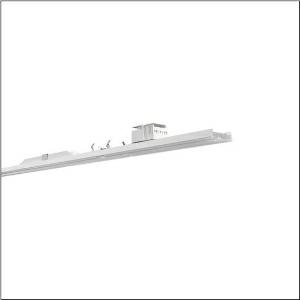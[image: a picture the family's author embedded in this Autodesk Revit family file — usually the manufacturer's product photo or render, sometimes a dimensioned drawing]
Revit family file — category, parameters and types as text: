
# Revit family: licross_r__11_recessed_mo_51tl12dn49xf_419c
name_source: partatom
category: Lighting Fixtures
units: mm (PartAtom-declared; Revit-internal decimal feet)

## family parameters
Cut with Voids When Loaded = No
Host = Face
Light Source = No
Part Type = Normal
Room Calculation Point = No
Round Connector Dimension = Use Diameter
Shared = No

## types (1)
- --- (1 x LED, 9140 lm, 55.4 W, 4000K)
    Apparent Load = 55 VA
    CIE Flux Codes = 67 92 99 100 100
    Color Rendering = 80
    Color Temperature = 4000K
    Default Elevation = 1800 mm
    Description = Licross® 11 Recessed MOluminaire insert, length: 1.500mm, width: 66mm, height: 67mm, LED rated luminous flux: 9.140lm, light colour: 840, control gear: DALI 2, control gear: ECG DALI, with plug, 5-pole, with phase selection, mains connection: 220..240V, AC, 50/60Hz, halogen-free wiring, primary optical cover: cover, of PMMA, light emission: direct distribution, protection rating (complete): IP40, insulation class (complete): insulation class I (protective earthing), certification: CE, ENEC, VDE, protection symbol: D if used in an environment without relevant dust loads with corresponding accessories, permissible ambient temperature for indoor applications: -25..+40°C, reducing of maximum allowable ambient temperature of 5°C with ceiling mounting, corresponds to IFS (International Featured Standards) requirements for safety and quality in the food industry, packaging unit: 1 piece
    Height = 58 mm
    Lamp = 1 x LED
    Lamp Light Flux = 9140 lm
    Lamp Power = 55.4 W
    Lamp count = 1
    Length = 1500 mm
    Luminous efficacy = 165 lm/W
    Manufacturer = Siteco
    ModVariant = No
    Model = 51TL12DN49XF
    Mounting Place = Ceiling
    Mounting Type = Pendant
    Number of Poles = 1
    OnlyDefault = Yes
    Power Factor = 1
    Product Name = Licross® 11 Recessed MO
    Product group = luminaire insert
    ProductGroupID = 902
    Protection Class = Protection class I
    Protection Degree = IP 40
    RLX_Detail_Level = 1
    RlxData = <blob elided: 22093 chars, md5=1f41e4fc>
    Socket = socket
    Standby Power = 0 W
    System Light Flux = 9140 lm
    System Power = 55 W
    Type Comments = factory setting: luminous flux: 100 % | dim-lin: 254 | 365 mA
    Type Image = l_1266722.jpg
    URL = http://relux.com
    VarID = @adj_139015
    Voltage = 0 V
    Weight = 0.00 kg
    Width = 66 mm

## geometry (parser evidence)
native form markers: Blend x4, Sweep x11
no freeform markers — native parametric forms only
